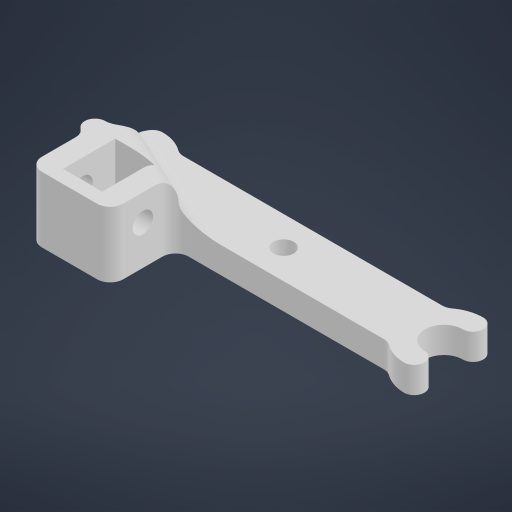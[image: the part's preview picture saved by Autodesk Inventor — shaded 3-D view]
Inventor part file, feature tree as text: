
AUTODESK INVENTOR PART (.ipt)
format: ipt  version: 2023 (Build 270158000, 158)  size: 280,064 bytes
history: native  units: mm
features: sketch x3, extrude x3, fillet x1
ambient origin geometry x8: Origin, YZ Plane, XZ Plane, XY Plane, X Axis, Y Axis, Z Axis, Center Point
bodies: Solid1 (feature_tree)
feature tree (7):
  sketch  "Sketch1"  dims[d0=20.0mm d2=49.0mm d3=10.0mm d5=10.0mm d7=12.0mm]
  sketch  "Sketch2"  dims[d9=3.1mm d10=4.0mm d11=0.0mm]
  extrude  "Extrusion1"  Depth=10.0mm
  extrude  "Extrusion3"  Depth=4.0mm TaperAngle=0.0deg
  extrude  "Extrusion4"  Depth=10.0mm
  fillet  "Fillet3"  Radius=6.212mm
  sketch  "Sketch4"  dims[d14=12.424mm d15=10.0mm d16=6.212mm d22=10.0mm d23=0.0mm d24=3.0mm d25=8.0mm d26=8.0mm d27=3.1mm d28=4.0mm d29=10.0mm d30=0.0mm d31=3.0mm d34=3.0mm d35=2.0mm d17=0.872665mm d36=0.0mm d37=0.0mm]
